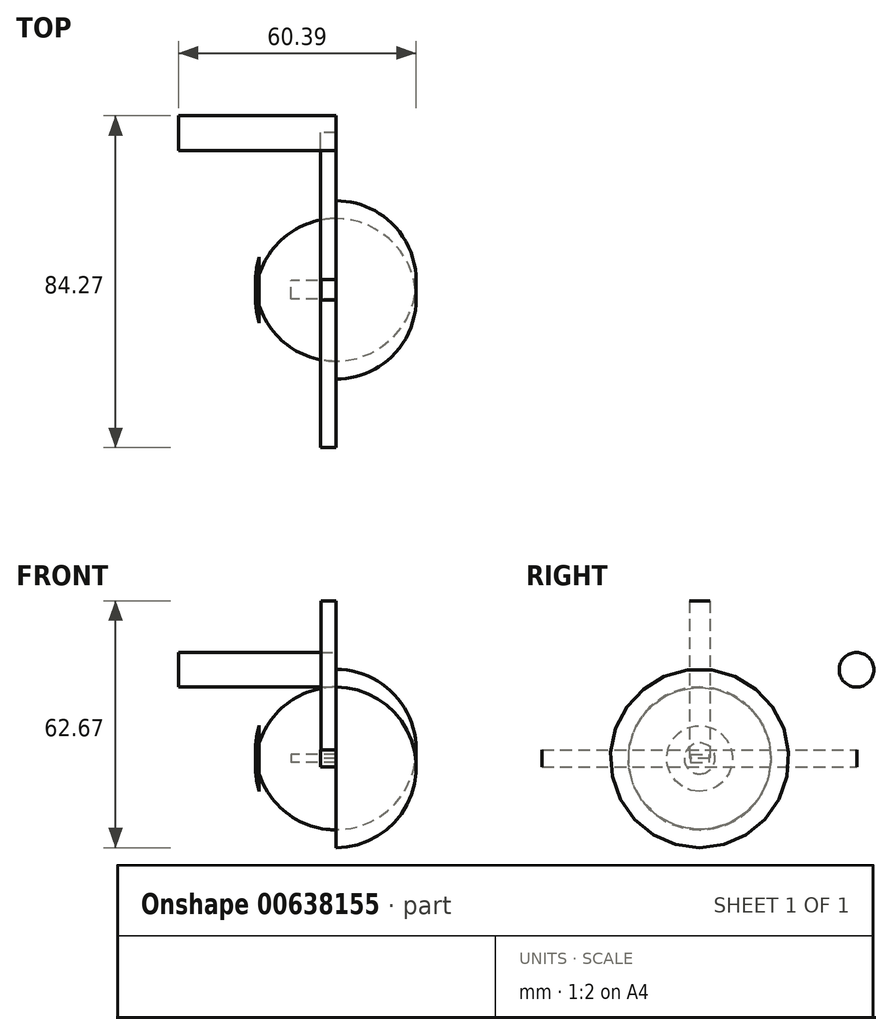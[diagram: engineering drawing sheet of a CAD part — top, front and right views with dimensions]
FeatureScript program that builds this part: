
annotation { "Feature Type Name" : "Feature", "Feature Type Description" : "" }
export const myFeature = defineFeature(function(context is Context, id is Id, definition is map)
    precondition{}
    {
        {
            var Q0;
            Q0=qCreatedBy(makeId("Top.planeOp"),FACE);
            var sketch = newSketch(context, id + "F0", { "sketchPlane" : qUnion([Q0])});
            skCircle(sketch, "E0", {"center": v(0, 0) * mm, "radius": 20.38 * mm});
            skSolve(sketch);
        }
        {
            var Q0;
            Q0=qCreatedBy(makeId("Top.planeOp"),FACE);
            var sketch = newSketch(context, id + "F1", { "sketchPlane" : qUnion([Q0])});
            skLineSegment(sketch, "E1.bottom", {"start": v(9.73, -2.27) * mm, "end": v(-11.39, -2.27) * mm});
            skLineSegment(sketch, "E1.top", {"start": v(9.73, 2.4) * mm, "end": v(-11.39, 2.4) * mm});
            skLineSegment(sketch, "E1.left", {"start": v(9.73, -2.27) * mm, "end": v(9.73, 2.4) * mm});
            skLineSegment(sketch, "E1.right", {"start": v(-11.39, -2.27) * mm, "end": v(-11.39, 2.4) * mm});
            skSolve(sketch);
        }
        {
            var Q0;
            Q0 = qSketchRegion(id + "F1", true);
            extrude(context, id + "F2", {"entities" : qUnion([Q0]), "endBound" : BoundingType.SYMMETRIC, "depth" : 2 * mm, "offsetDistance" : 25 * mm});
        }
        {
            var Q0;
            Q0 = qSketchRegion(id + "F0", true);
            var Q1;
            Q1=makeQuery(id+"F2.opExtrude","CAP_EDGE",EDGE,{"disambiguationData":[OSD([sQuery(id+"F1.wireOp",EDGE,"E1.bottom")])],"isStart":true});
            revolve(context, id + "F3", {"entities" : qUnion([Q0]), "axis" : qUnion([Q1]), "revolveType" : RevolveType.FULL});
        }
        {
            var Q0;
            Q0=qCreatedBy(makeId("Top.planeOp"),FACE);
            var sketch = newSketch(context, id + "F4", { "sketchPlane" : qUnion([Q0])});
            skLineSegment(sketch, "E2.bottom", {"start": v(29.24, 26.33) * mm, "end": v(0, 26.33) * mm});
            skLineSegment(sketch, "E2.top", {"start": v(29.24, -30.8) * mm, "end": v(0, -30.8) * mm});
            skLineSegment(sketch, "E2.left", {"start": v(29.24, 26.33) * mm, "end": v(29.24, -30.8) * mm});
            skLineSegment(sketch, "E2.right", {"start": v(0, 26.33) * mm, "end": v(0, -30.8) * mm});
            skSolve(sketch);
        }
        {
            var Q0;
            Q0 = qSketchRegion(id + "F4", true);
            extrude(context, id + "F5", {"entities" : qUnion([Q0]), "operationType" : NewBodyOperationType.REMOVE, "endBound" : BoundingType.SYMMETRIC, "oppositeDirection" : true, "depth" : 50 * mm, "offsetDistance" : 25 * mm});
        }
        {
            var Q0;
            Q0=qCreatedBy(makeId("Front.planeOp"),FACE);
            var sketch = newSketch(context, id + "F6", { "sketchPlane" : qUnion([Q0])});
            skLineSegment(sketch, "E3.bottom", {"start": v(0, 2.23) * mm, "end": v(-3.84, 2.23) * mm});
            skLineSegment(sketch, "E3.top", {"start": v(0, -2.2) * mm, "end": v(-3.84, -2.2) * mm});
            skLineSegment(sketch, "E3.left", {"start": v(0, 2.23) * mm, "end": v(0, -2.2) * mm});
            skLineSegment(sketch, "E3.right", {"start": v(-3.84, 2.23) * mm, "end": v(-3.84, -2.2) * mm});
            skSolve(sketch);
        }
        {
            var Q0;
            Q0 = qSketchRegion(id + "F6", true);
            extrude(context, id + "F7", {"entities" : qUnion([Q0]), "endBound" : BoundingType.SYMMETRIC, "depth" : 80 * mm, "offsetDistance" : 25 * mm});
        }
        {
            var Q0;
            Q0=qCreatedBy(makeId("Top.planeOp"),FACE);
            var sketch = newSketch(context, id + "F8", { "sketchPlane" : qUnion([Q0])});
            skLineSegment(sketch, "E4.bottom", {"start": v(0, 2.63) * mm, "end": v(-3.8, 2.63) * mm});
            skLineSegment(sketch, "E4.top", {"start": v(0, -2.57) * mm, "end": v(-3.8, -2.57) * mm});
            skLineSegment(sketch, "E4.left", {"start": v(0, 2.63) * mm, "end": v(0, -2.57) * mm});
            skLineSegment(sketch, "E4.right", {"start": v(-3.8, 2.63) * mm, "end": v(-3.8, -2.57) * mm});
            skSolve(sketch);
        }
        {
            var Q0;
            Q0 = qSketchRegion(id + "F8", true);
            var Q1;
            Q1=sQuery(id+"F8.wireOp",EDGE,"E4.bottom");
            var Q2;
            Q2=sQuery(id+"F8.wireOp",EDGE,"E4.top");
            var Q3;
            Q3=sQuery(id+"F8.wireOp",EDGE,"E4.left");
            var Q4;
            Q4=sQuery(id+"F8.wireOp",EDGE,"E4.right");
            extrude(context, id + "F9", {"entities" : qUnion([Q0]), "surfaceEntities" : qUnion([Q1, Q2, Q3, Q4]), "depth" : 40 * mm, "offsetDistance" : 25 * mm});
        }
        {
            var Q0;
            Q0=makeQuery(id+"F3.opRevolve","SWEPT_BODY",BODY,{"disambiguationData":[OSD([sQuery(id+"F0.wireOp",EDGE,"E0")])]});
            transform(context, id + "F10", {"entities" : qUnion([Q0]), "transformType" : TransformType.TRANSLATION_3D, "dx" : 0 * mm, "dy" : 2.3 * mm, "dz" : 0 * mm, "makeCopy" : false});
        }
        {
            var Q0;
            Q0=makeQuery(id+"F3.opRevolve","SWEPT_BODY",BODY,{"disambiguationData":[OSD([sQuery(id+"F0.wireOp",EDGE,"E0")])]});
            transform(context, id + "F11", {"entities" : qUnion([Q0]), "transformType" : TransformType.TRANSLATION_3D, "dx" : 0 * mm, "dy" : 0 * mm, "dz" : 1 * mm, "makeCopy" : false});
        }
        {
            var Q0;
            Q0=qCreatedBy(makeId("Top.planeOp"),FACE);
            var sketch = newSketch(context, id + "F12", { "sketchPlane" : qUnion([Q0])});
            skLineSegment(sketch, "E5.bottom", {"start": v(-19.46, 11.41) * mm, "end": v(-28.36, 11.41) * mm});
            skLineSegment(sketch, "E5.top", {"start": v(-19.46, -14) * mm, "end": v(-28.36, -14) * mm});
            skLineSegment(sketch, "E5.left", {"start": v(-19.46, 11.41) * mm, "end": v(-19.46, -14) * mm});
            skLineSegment(sketch, "E5.right", {"start": v(-28.36, 11.41) * mm, "end": v(-28.36, -14) * mm});
            skSolve(sketch);
        }
        {
            var Q0;
            Q0 = qSketchRegion(id + "F12", true);
            extrude(context, id + "F13", {"entities" : qUnion([Q0]), "operationType" : NewBodyOperationType.REMOVE, "endBound" : BoundingType.SYMMETRIC, "oppositeDirection" : true, "depth" : 25 * mm, "offsetDistance" : 25 * mm});
        }
        {
            var Q0;
            Q0=qCreatedBy(makeId("Right.planeOp"),FACE);
            var sketch = newSketch(context, id + "F14", { "sketchPlane" : qUnion([Q0])});
            skCircle(sketch, "E6", {"center": v(39.88, 22.52) * mm, "radius": 4.4 * mm});
            skSolve(sketch);
        }
        {
            var Q0;
            Q0 = qSketchRegion(id + "F14", true);
            extrude(context, id + "F15", {"entities" : qUnion([Q0]), "oppositeDirection" : true, "depth" : 40 * mm, "offsetDistance" : 25 * mm});
        }
    });
